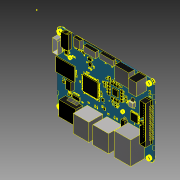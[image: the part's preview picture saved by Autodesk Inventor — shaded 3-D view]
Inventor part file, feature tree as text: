
AUTODESK INVENTOR PART (.ipt)
format: ipt  version: 2015 (Build 190159000, 159)  size: 3,822,592 bytes
history: native  units: in
note: dims shown in document units (in); Inventor stores cm internally (conversion verified against a paired STEP export)
features: sketch x4, other x3, extrude x2, fillet x1, hole x1, projected_geometry x1
ambient origin geometry x8: Origin, YZ Plane, XZ Plane, XY Plane, X Axis, Y Axis, Z Axis, Center Point
bodies: Solid1 (feature_tree)
feature tree (12):
  other  "[3D] ODROID-XU"
  extrude  "Extrusion1"  Depth=2.748in
  sketch  "Sketch4"  dims[d9=2.748in d10=0.0394in d11=0.0in]
  fillet  "Fillet1"  Radius=3.7008in
  extrude  "Extrusion2"  Depth=0.0394in TaperAngle=0.0deg
  hole  "Hole1"  [1 undecoded]
  sketch  "Sketch2"  dims[d0=3.7008in d1=2.748in d8=3.7008in]
  sketch  "Sketch5"  dims[d12=0.1339in d13=0.0394in d14=0.0in]
  projected_geometry  "Projected Loop1"
  sketch  "Sketch6"  dims[d15=3.4252in d16=2.748in d17=3.7008in d18=3.4252in d19=3.4252in d20=2.4803in d21=2.4803in d22=0.1575in d23=0.1575in d24=0.1575in d25=0.1575in d26=0.1417in d27=0.2953in d28=0.248in d29=0.0984in d30=90.0deg d31=0.3937in d32=0.8108in]
  other  "MeshFeature1"
  other  "Srf1"
note: 1 required parameter value undecoded (feature->parameter linkage not recoverable at this tier; creation-order binding heuristic only, values carry confidence <= 0.55)
